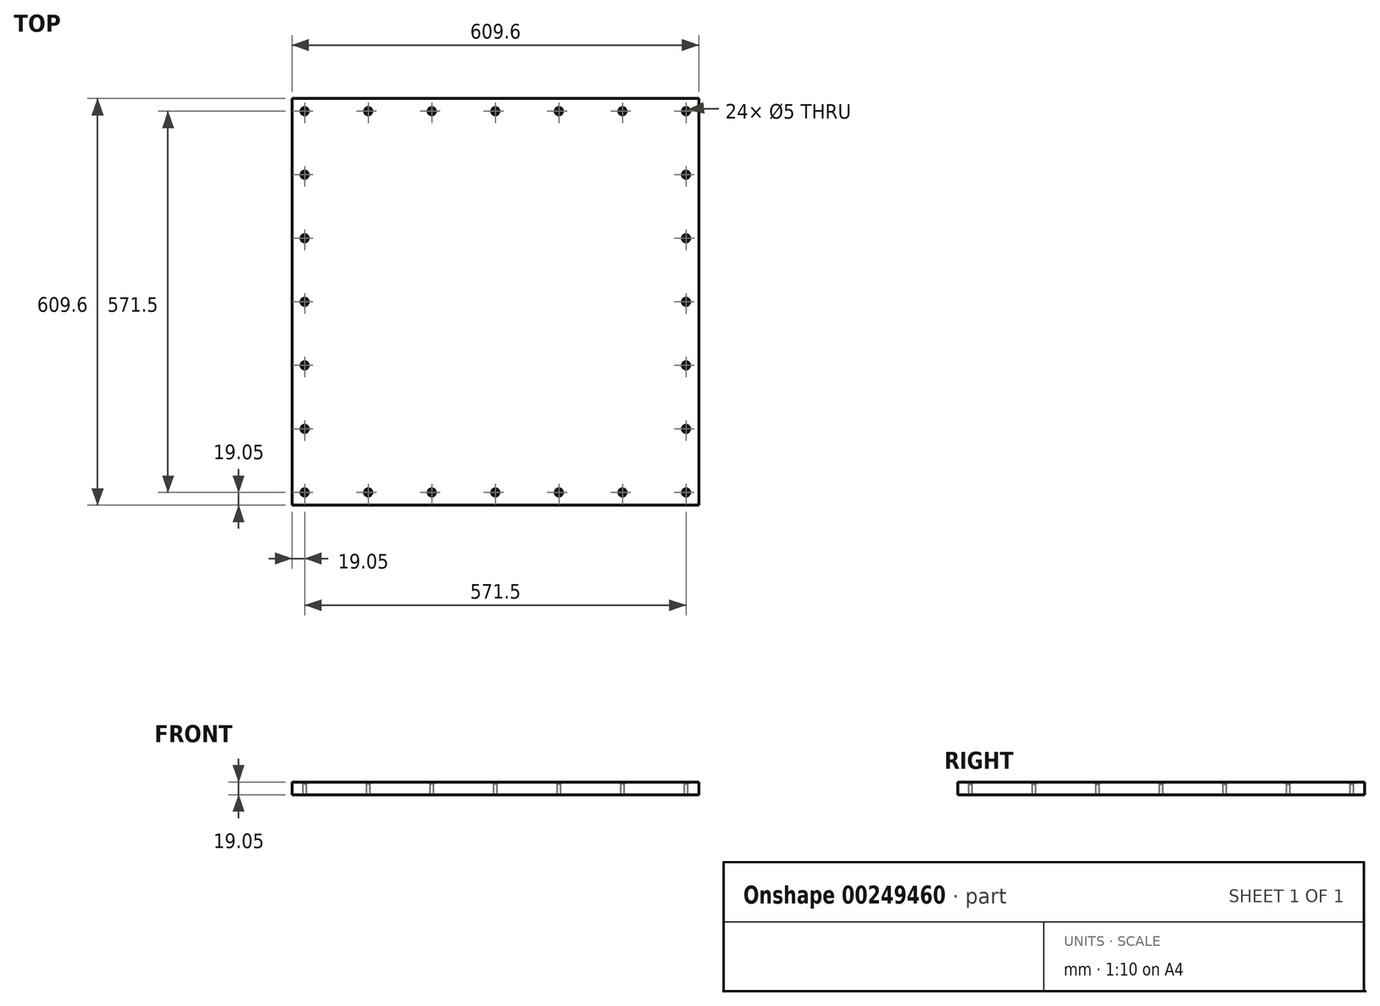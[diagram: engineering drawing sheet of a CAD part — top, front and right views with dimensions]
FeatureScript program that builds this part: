
annotation { "Feature Type Name" : "Feature", "Feature Type Description" : "" }
export const myFeature = defineFeature(function(context is Context, id is Id, definition is map)
    precondition{}
    {
        {
            var Q0;
            Q0=qCreatedBy(makeId("Top.planeOp"),FACE);
            var sketch = newSketch(context, id + "F0", { "sketchPlane" : qUnion([Q0])});
            skLineSegment(sketch, "E0.bottom", {"start": v(0, 0) * mm, "end": v(609.6, 0) * mm});
            skLineSegment(sketch, "E0.top", {"start": v(0, 609.6) * mm, "end": v(609.6, 609.6) * mm});
            skLineSegment(sketch, "E0.left", {"start": v(0, 0) * mm, "end": v(0, 609.6) * mm});
            skLineSegment(sketch, "E0.right", {"start": v(609.6, 0) * mm, "end": v(609.6, 609.6) * mm});
            skSolve(sketch);
        }
        {
            var Q0;
            Q0 = qSketchRegion(id + "F0", true);
            extrude(context, id + "F1", {"entities" : qUnion([Q0]), "depth" : 19.05 * mm});
        }
        {
            var Q0;
            Q0=makeQuery(id+"F1.opExtrude","CAP_FACE",FACE,{"disambiguationData":[OSD([sQuery(id+"F0.wireOp",EDGE,"E0.bottom"),sQuery(id+"F0.wireOp",EDGE,"E0.top"),sQuery(id+"F0.wireOp",EDGE,"E0.left"),sQuery(id+"F0.wireOp",EDGE,"E0.right")])],"isStart":false});
            var sketch = newSketch(context, id + "F2", { "sketchPlane" : qUnion([Q0])});
            skLineSegment(sketch, "E1", {"start": v(304.8, 609.6) * mm, "end": v(304.8, 0) * mm, "construction": true});
            skLineSegment(sketch, "E2", {"start": v(0, 304.8) * mm, "end": v(609.6, 304.8) * mm, "construction": true});
            skLineSegment(sketch, "E3", {"start": v(19.05, 304.8) * mm, "end": v(19.05, 400.05) * mm});
            skLineSegment(sketch, "E4", {"start": v(19.05, 400.05) * mm, "end": v(19.05, 495.3) * mm});
            skLineSegment(sketch, "E5", {"start": v(19.05, 495.3) * mm, "end": v(19.05, 590.55) * mm});
            skLineSegment(sketch, "E6", {"start": v(19.05, 590.55) * mm, "end": v(114.3, 590.55) * mm});
            skLineSegment(sketch, "E7", {"start": v(114.3, 590.55) * mm, "end": v(209.55, 590.55) * mm});
            skLineSegment(sketch, "E8", {"start": v(209.55, 590.55) * mm, "end": v(304.8, 590.55) * mm});
            skLineSegment(sketch, "E9.MirrorCS", {"start": v(400.05, 590.55) * mm, "end": v(304.8, 590.55) * mm});
            skLineSegment(sketch, "E10.MirrorCS", {"start": v(495.3, 590.55) * mm, "end": v(400.05, 590.55) * mm});
            skLineSegment(sketch, "E11.MirrorCS", {"start": v(590.55, 590.55) * mm, "end": v(495.3, 590.55) * mm});
            skLineSegment(sketch, "E12.MirrorCS", {"start": v(590.55, 495.3) * mm, "end": v(590.55, 590.55) * mm});
            skLineSegment(sketch, "E13.MirrorCS", {"start": v(590.55, 304.8) * mm, "end": v(590.55, 400.05) * mm});
            skLineSegment(sketch, "E14.MirrorCS", {"start": v(590.55, 400.05) * mm, "end": v(590.55, 495.3) * mm});
            skLineSegment(sketch, "E15.MirrorCS", {"start": v(114.3, 19.05) * mm, "end": v(209.55, 19.05) * mm});
            skLineSegment(sketch, "E16.MirrorCS", {"start": v(19.05, 19.05) * mm, "end": v(114.3, 19.05) * mm});
            skLineSegment(sketch, "E17.MirrorCS", {"start": v(19.05, 114.3) * mm, "end": v(19.05, 19.05) * mm});
            skLineSegment(sketch, "E18.MirrorCS", {"start": v(19.05, 209.55) * mm, "end": v(19.05, 114.3) * mm});
            skLineSegment(sketch, "E19.MirrorCS", {"start": v(19.05, 304.8) * mm, "end": v(19.05, 209.55) * mm});
            skLineSegment(sketch, "E20.MirrorCS", {"start": v(590.55, 209.55) * mm, "end": v(590.55, 114.3) * mm});
            skLineSegment(sketch, "E21.MirrorCS", {"start": v(209.55, 19.05) * mm, "end": v(304.8, 19.05) * mm});
            skLineSegment(sketch, "E22.MirrorCS", {"start": v(400.05, 19.05) * mm, "end": v(304.8, 19.05) * mm});
            skLineSegment(sketch, "E23.MirrorCS", {"start": v(495.3, 19.05) * mm, "end": v(400.05, 19.05) * mm});
            skLineSegment(sketch, "E24.MirrorCS", {"start": v(590.55, 19.05) * mm, "end": v(495.3, 19.05) * mm});
            skLineSegment(sketch, "E25.MirrorCS", {"start": v(590.55, 114.3) * mm, "end": v(590.55, 19.05) * mm});
            skLineSegment(sketch, "E26.MirrorCS", {"start": v(590.55, 304.8) * mm, "end": v(590.55, 209.55) * mm});
            skSolve(sketch);
        }
        {
            var Q0;
            Q0=sQuery(id+"F2.wireOp",VERTEX,"E3.start");
            var Q1;
            Q1=sQuery(id+"F2.wireOp",VERTEX,"E4.start");
            var Q2;
            Q2=sQuery(id+"F2.wireOp",VERTEX,"E5.start");
            var Q3;
            Q3=sQuery(id+"F2.wireOp",VERTEX,"E6.start");
            var Q4;
            Q4=sQuery(id+"F2.wireOp",VERTEX,"E7.start");
            var Q5;
            Q5=sQuery(id+"F2.wireOp",VERTEX,"E8.start");
            var Q6;
            Q6=sQuery(id+"F2.wireOp",VERTEX,"E8.end");
            var Q7;
            Q7=sQuery(id+"F2.wireOp",VERTEX,"E9.MirrorCS.start");
            var Q8;
            Q8=sQuery(id+"F2.wireOp",VERTEX,"E10.MirrorCS.start");
            var Q9;
            Q9=sQuery(id+"F2.wireOp",VERTEX,"E11.MirrorCS.start");
            var Q10;
            Q10=sQuery(id+"F2.wireOp",VERTEX,"E12.MirrorCS.start");
            var Q11;
            Q11=sQuery(id+"F2.wireOp",VERTEX,"E14.MirrorCS.start");
            var Q12;
            Q12=sQuery(id+"F2.wireOp",VERTEX,"E26.MirrorCS.start");
            var Q13;
            Q13=sQuery(id+"F2.wireOp",VERTEX,"E20.MirrorCS.start");
            var Q14;
            Q14=sQuery(id+"F2.wireOp",VERTEX,"E20.MirrorCS.end");
            var Q15;
            Q15=sQuery(id+"F2.wireOp",VERTEX,"E25.MirrorCS.end");
            var Q16;
            Q16=sQuery(id+"F2.wireOp",VERTEX,"E24.MirrorCS.end");
            var Q17;
            Q17=sQuery(id+"F2.wireOp",VERTEX,"E23.MirrorCS.end");
            var Q18;
            Q18=sQuery(id+"F2.wireOp",VERTEX,"E21.MirrorCS.end");
            var Q19;
            Q19=sQuery(id+"F2.wireOp",VERTEX,"E15.MirrorCS.end");
            var Q20;
            Q20=sQuery(id+"F2.wireOp",VERTEX,"E16.MirrorCS.end");
            var Q21;
            Q21=sQuery(id+"F2.wireOp",VERTEX,"E17.MirrorCS.end");
            var Q22;
            Q22=sQuery(id+"F2.wireOp",VERTEX,"E18.MirrorCS.end");
            var Q23;
            Q23=sQuery(id+"F2.wireOp",VERTEX,"E18.MirrorCS.start");
            var Q24;
            Q24=sQuery(id+"F2.wireOp",VERTEX,"E18.MirrorCS.end");
            var Q25;
            Q25=makeQuery(id+"F1.opExtrude","SWEPT_BODY",BODY,{"disambiguationData":[OSD([sQuery(id+"F0.wireOp",EDGE,"E0.bottom"),sQuery(id+"F0.wireOp",EDGE,"E0.top"),sQuery(id+"F0.wireOp",EDGE,"E0.left"),sQuery(id+"F0.wireOp",EDGE,"E0.right")])]});
            hole(context, id + "F3", {"style" : HoleStyle.C_SINK, "endStyle" : HoleEndStyle.THROUGH, "standardTappedOrClearance" : lookupTablePath({ "standard" : "ISO", "size" : "5", "type" : "Drilled" }), "standardBlindInLast" : lookupTablePath({ "standard" : "ISO", "size" : "5", "type" : "Drilled" }), "holeDiameter" : 5 * mm, "cSinkDiameter" : 11.2 * mm, "cSinkAngle" : 90 * degree, "tappedDepth" : 12.7 * mm, "tapClearance" : 3, "startFromSketch" : true, "locations" : qUnion([Q0, Q1, Q2, Q3, Q4, Q5, Q6, Q7, Q8, Q9, Q10, Q11, Q12, Q13, Q14, Q15, Q16, Q17, Q18, Q19, Q20, Q21, Q22, Q23, Q24]), "scope" : qUnion([Q25])});
        }
    });
